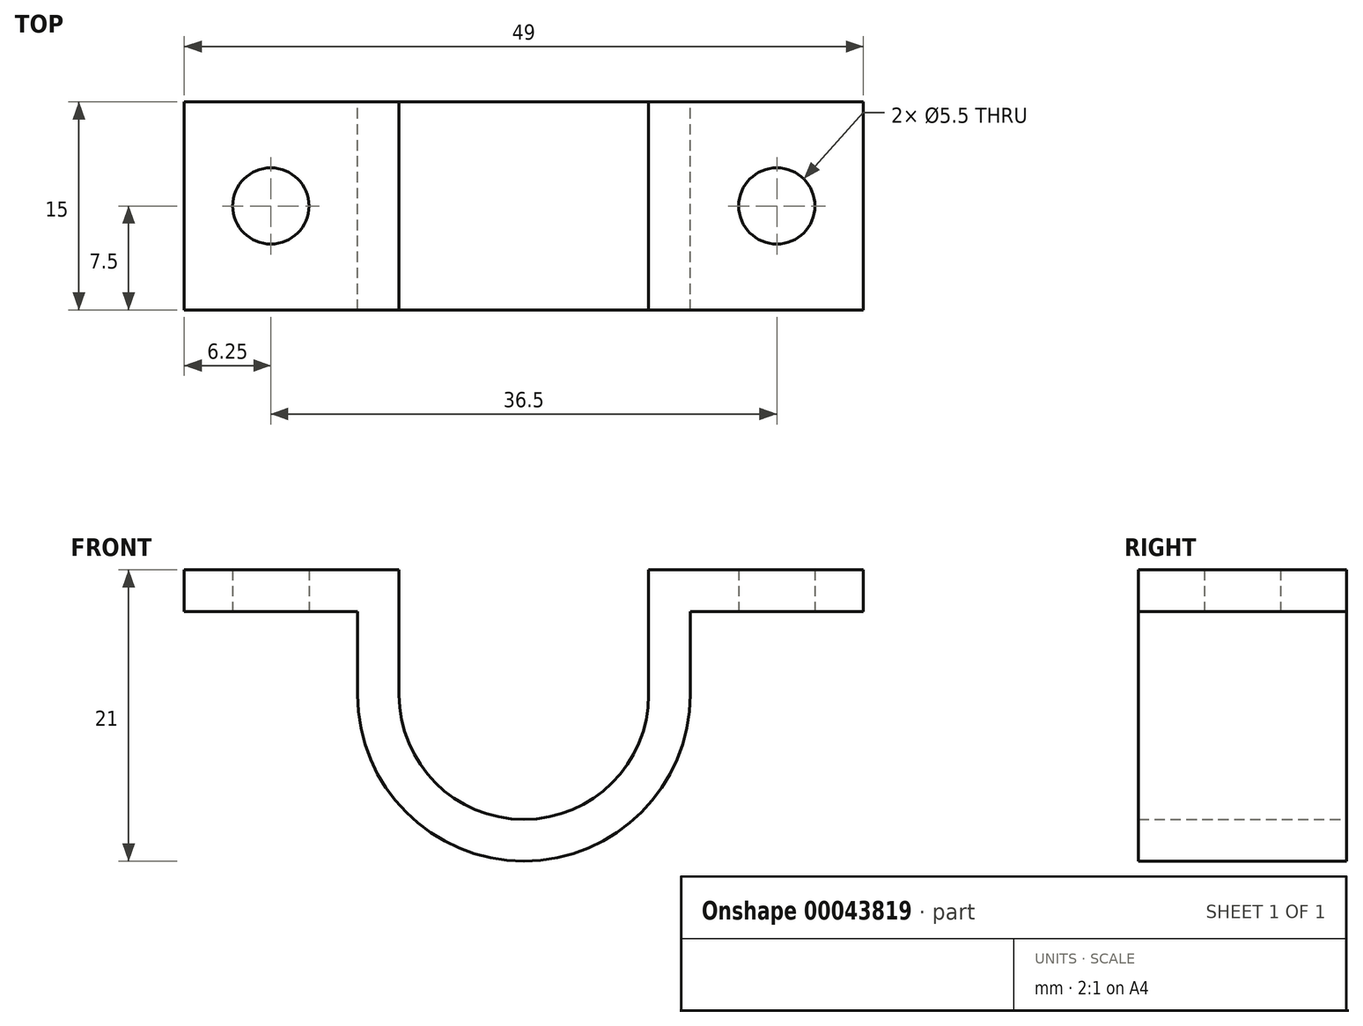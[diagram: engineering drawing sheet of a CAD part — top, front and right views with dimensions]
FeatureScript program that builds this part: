
annotation { "Feature Type Name" : "Feature", "Feature Type Description" : "" }
export const myFeature = defineFeature(function(context is Context, id is Id, definition is map)
    precondition{}
    {
        {
            var Q0;
            Q0=qCreatedBy(makeId("Front.planeOp"),FACE);
            var sketch = newSketch(context, id + "F0", { "sketchPlane" : qUnion([Q0])});
            skArc(sketch, "E0", {"start": v(-9, 0) * mm, "mid": v(0, -9) * mm, "end": v(9, 0) * mm});
            skArc(sketch, "E1", {"start": v(-12, 0) * mm, "mid": v(0, -12) * mm, "end": v(12, 0) * mm});
            skLineSegment(sketch, "E2.bottom", {"start": v(-12, 0) * mm, "end": v(-9, 0) * mm, "construction": true});
            skLineSegment(sketch, "E2.top", {"start": v(-12, 9) * mm, "end": v(-9, 9) * mm});
            skLineSegment(sketch, "E2.left", {"start": v(-12, 0) * mm, "end": v(-12, 6) * mm});
            skLineSegment(sketch, "E2.right", {"start": v(12, 0) * mm, "end": v(12, 6) * mm});
            skLineSegment(sketch, "E3", {"start": v(-9, 0) * mm, "end": v(-9, 9) * mm});
            skLineSegment(sketch, "E4", {"start": v(9, 0) * mm, "end": v(9, 9) * mm});
            skLineSegment(sketch, "E5.bottom", {"start": v(-12, 9) * mm, "end": v(-24.5, 9) * mm});
            skLineSegment(sketch, "E5.top", {"start": v(-12, 6) * mm, "end": v(-24.5, 6) * mm});
            skLineSegment(sketch, "E5.left", {"start": v(-12, 9) * mm, "end": v(-12, 6) * mm, "construction": true});
            skLineSegment(sketch, "E5.right", {"start": v(-24.5, 9) * mm, "end": v(-24.5, 6) * mm});
            skLineSegment(sketch, "E6.bottom", {"start": v(12, 9) * mm, "end": v(24.5, 9) * mm});
            skLineSegment(sketch, "E6.top", {"start": v(12, 6) * mm, "end": v(24.5, 6) * mm});
            skLineSegment(sketch, "E6.right", {"start": v(24.5, 9) * mm, "end": v(24.5, 6) * mm});
            skLineSegment(sketch, "E7.trimOffspring", {"start": v(9, 9) * mm, "end": v(12, 9) * mm});
            skLineSegment(sketch, "E8.trimOffspring", {"start": v(9, 0) * mm, "end": v(12, 0) * mm, "construction": true});
            skSolve(sketch);
        }
        {
            var Q0;
            Q0 = qSketchRegion(id + "F0", true);
            extrude(context, id + "F1", {"entities" : qUnion([Q0]), "depth" : 15 * mm});
        }
        {
            var Q0;
            Q0=makeQuery(id+"F1.opExtrude","SWEPT_FACE",FACE,{"disambiguationData":[OSD([sQuery(id+"F0.wireOp",EDGE,"E5.top")])]});
            var sketch = newSketch(context, id + "F2", { "sketchPlane" : qUnion([Q0])});
            skLineSegment(sketch, "E9.0", {"start": v(-12, 15) * mm, "end": v(-24.5, 15) * mm});
            skLineSegment(sketch, "E10.0", {"start": v(-12, 0) * mm, "end": v(-24.5, 0) * mm});
            skLineSegment(sketch, "E11.0", {"start": v(12, 0) * mm, "end": v(24.5, 0) * mm});
            skLineSegment(sketch, "E12.0", {"start": v(12, 15) * mm, "end": v(24.5, 15) * mm});
            skLineSegment(sketch, "E13.0", {"start": v(24.5, 15) * mm, "end": v(24.5, 0) * mm});
            skLineSegment(sketch, "E14.0", {"start": v(-24.5, 15) * mm, "end": v(-24.5, 0) * mm});
            skLineSegment(sketch, "E15", {"start": v(-18.25, 15) * mm, "end": v(-18.25, 0) * mm, "construction": true});
            skLineSegment(sketch, "E16", {"start": v(18.25, 15) * mm, "end": v(18.25, 0) * mm, "construction": true});
            skCircle(sketch, "E17", {"center": v(18.25, 7.5) * mm, "radius": 2.75 * mm});
            skCircle(sketch, "E18", {"center": v(-18.25, 7.5) * mm, "radius": 2.75 * mm});
            skSolve(sketch);
        }
        {
            var Q0;
            Q0 = qSketchRegion(id + "F2", true);
            extrude(context, id + "F3", {"entities" : qUnion([Q0]), "operationType" : NewBodyOperationType.REMOVE, "oppositeDirection" : true, "depth" : 25 * mm});
        }
    });
